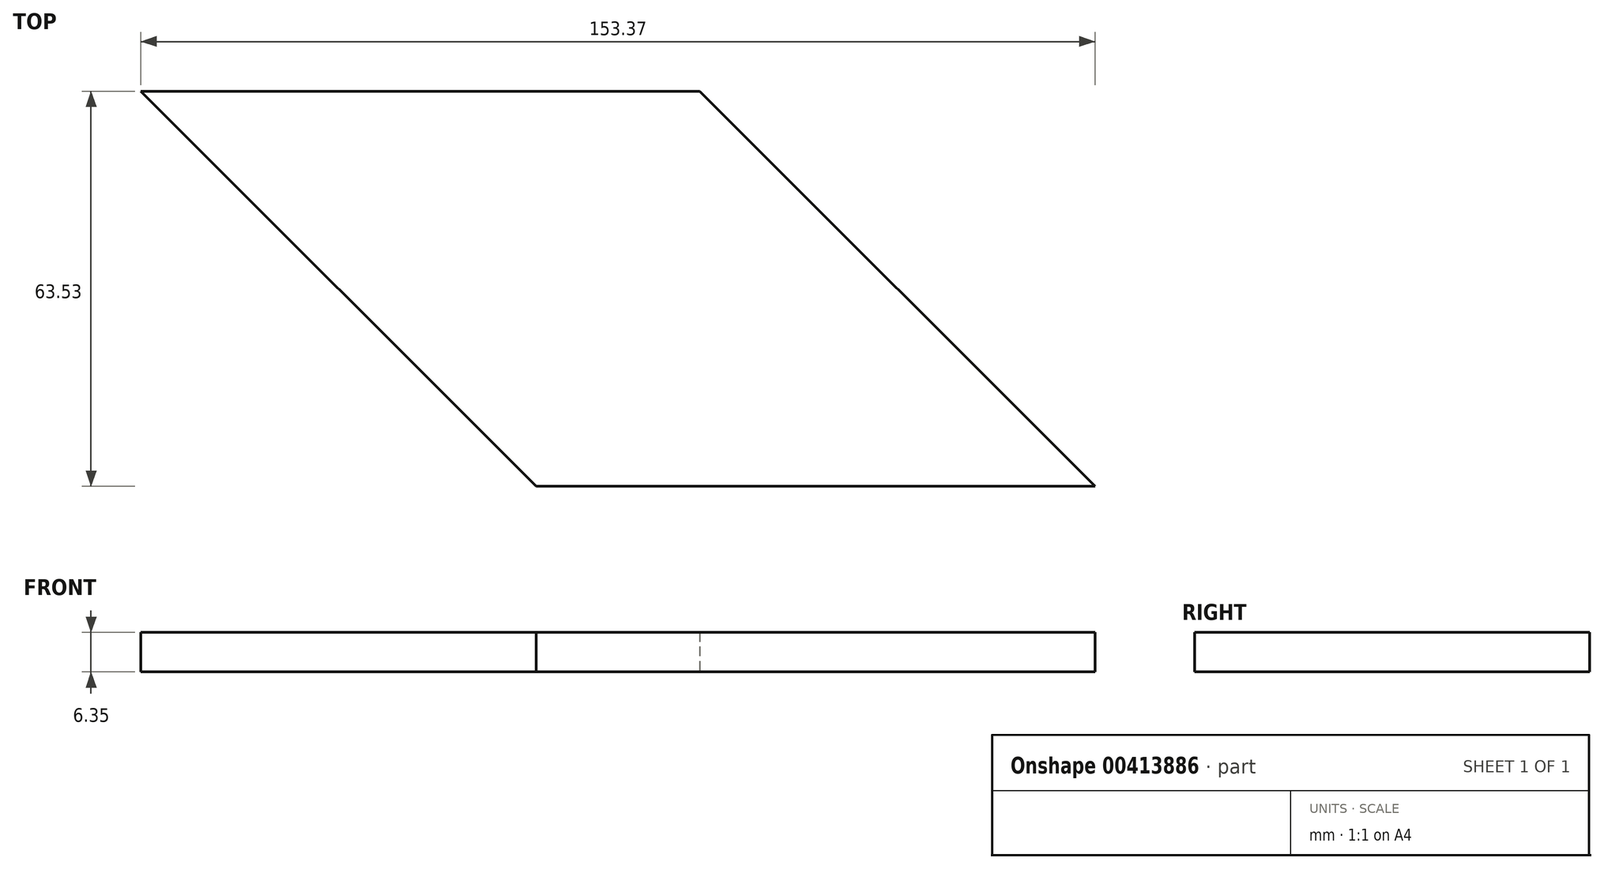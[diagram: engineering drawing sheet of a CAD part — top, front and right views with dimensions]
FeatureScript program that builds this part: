
annotation { "Feature Type Name" : "Feature", "Feature Type Description" : "" }
export const myFeature = defineFeature(function(context is Context, id is Id, definition is map)
    precondition{}
    {
        {
            var Q0;
            Q0=qCreatedBy(makeId("Top.planeOp"),FACE);
            var sketch = newSketch(context, id + "F0", { "sketchPlane" : qUnion([Q0])});
            skLineSegment(sketch, "E0", {"start": v(-71.88, 0) * mm, "end": v(-122.71, 50.83) * mm, "construction": true});
            skLineSegment(sketch, "E1", {"start": v(-122.71, 50.83) * mm, "end": v(-50.83, 50.83) * mm, "construction": true});
            skLineSegment(sketch, "E2", {"start": v(-50.83, 50.83) * mm, "end": v(0, 0) * mm, "construction": true});
            skLineSegment(sketch, "E3.1.0", {"start": v(-71.88, 0) * mm, "end": v(0, 0) * mm, "construction": true});
            skLineSegment(sketch, "E4.0", {"start": v(-138.04, 57.18) * mm, "end": v(-48.2, 57.18) * mm});
            skLineSegment(sketch, "E4.1", {"start": v(-74.51, -6.35) * mm, "end": v(-138.04, 57.18) * mm});
            skLineSegment(sketch, "E4.2", {"start": v(-74.51, -6.35) * mm, "end": v(15.33, -6.35) * mm});
            skLineSegment(sketch, "E4.3", {"start": v(-48.2, 57.18) * mm, "end": v(15.33, -6.35) * mm});
            skSolve(sketch);
        }
        {
            var Q0;
            Q0 = qSketchRegion(id + "F0", true);
            extrude(context, id + "F1", {"entities" : qUnion([Q0]), "flatOperationType" : FlatOperationType.REMOVE, "offsetDistance" : 25.4 * mm, "depth" : 6.35 * mm, "domain" : OperationDomain.MODEL});
        }
    });
